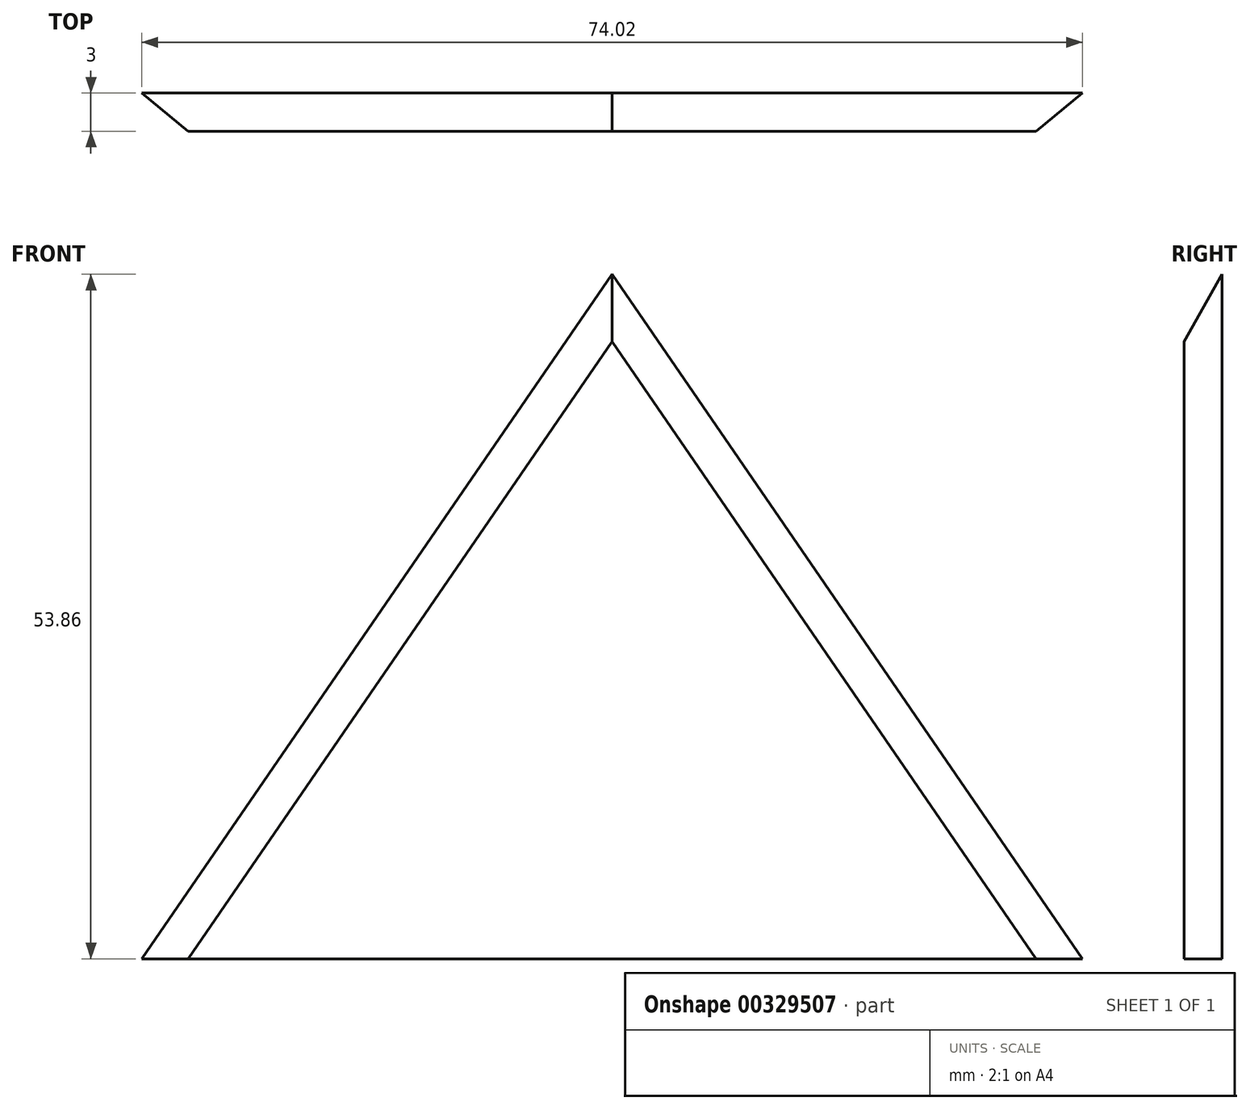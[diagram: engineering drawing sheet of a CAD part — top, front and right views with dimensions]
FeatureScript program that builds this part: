
annotation { "Feature Type Name" : "Feature", "Feature Type Description" : "" }
export const myFeature = defineFeature(function(context is Context, id is Id, definition is map)
    precondition{}
    {
        {
            var Q0;
            Q0=qCreatedBy(makeId("Front.planeOp"),FACE);
            var sketch = newSketch(context, id + "F0", { "sketchPlane" : qUnion([Q0])});
            skLineSegment(sketch, "E0", {"start": v(-39.43, 0) * mm, "end": v(0, 57.39) * mm});
            skLineSegment(sketch, "E1", {"start": v(0, 57.39) * mm, "end": v(39.43, 0) * mm});
            skLineSegment(sketch, "E2", {"start": v(39.43, 0) * mm, "end": v(-39.43, 0) * mm});
            skSolve(sketch);
        }
        {
            var Q0;
            Q0=makeQuery(id+"F0.imprint","IMPRINT",FACE,{"disambiguationData":[TD([[makeQuery(id+"F0.imprint","IMPRINT",EDGE,{"derivedFrom":sQuery(id+"F0.wireOp",EDGE,"E0")}),-1.0]])]});
            extrude(context, id + "F1", {"entities" : qUnion([Q0]), "endBound" : BoundingType.SYMMETRIC, "depth" : 3 * mm});
        }
        {
            var Q0;
            Q0=makeQuery(id+"F1.opExtrude","CAP_EDGE",EDGE,{"disambiguationData":[OSD([sQuery(id+"F0.wireOp",EDGE,"E0")])],"isStart":false});
            var Q1;
            Q1=makeQuery(id+"F1.opExtrude","CAP_EDGE",EDGE,{"disambiguationData":[OSD([sQuery(id+"F0.wireOp",EDGE,"E1")])],"isStart":false});
            chamfer(context, id + "F2", {"entities" : qUnion([Q0, Q1]), "width" : 5 * mm, "tangentPropagation" : true});
        }
    });
